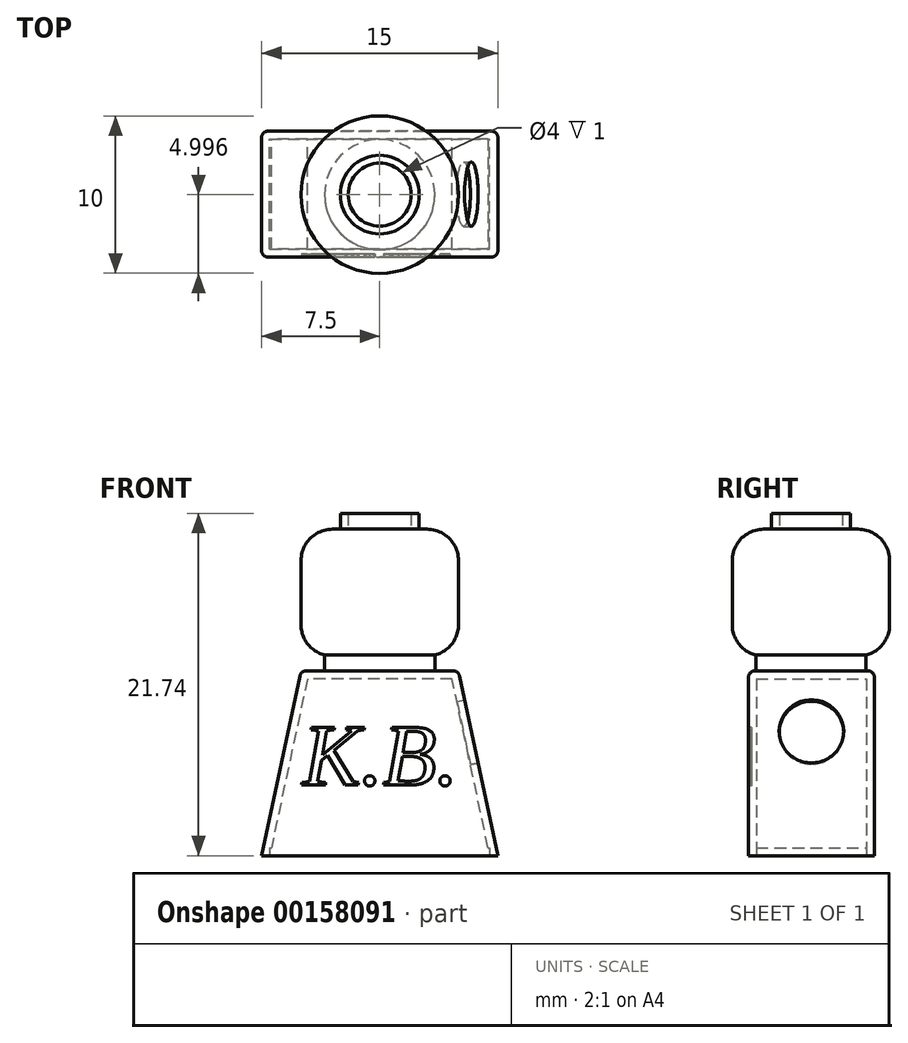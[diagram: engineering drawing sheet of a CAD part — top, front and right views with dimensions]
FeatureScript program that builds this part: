
annotation { "Feature Type Name" : "Feature", "Feature Type Description" : "" }
export const myFeature = defineFeature(function(context is Context, id is Id, definition is map)
    precondition{}
    {
        {
            var Q0;
            Q0=qCreatedBy(makeId("Front.planeOp"),FACE);
            var sketch = newSketch(context, id + "F0", { "sketchPlane" : qUnion([Q0])});
            skLineSegment(sketch, "E0", {"start": v(0, 11.74) * mm, "end": v(-5, 11.74) * mm});
            skLineSegment(sketch, "E1", {"start": v(-5, 11.74) * mm, "end": v(-7.5, 0) * mm});
            skLineSegment(sketch, "E2", {"start": v(-7.5, 0) * mm, "end": v(0, 0) * mm});
            skLineSegment(sketch, "E3", {"start": v(0, 0) * mm, "end": v(7.5, 0) * mm});
            skLineSegment(sketch, "E4", {"start": v(7.5, 0) * mm, "end": v(5, 11.74) * mm});
            skLineSegment(sketch, "E5", {"start": v(5, 11.74) * mm, "end": v(0, 11.74) * mm});
            skSolve(sketch);
        }
        {
            var Q0;
            Q0=makeQuery(id+"F0.imprint","IMPRINT",FACE,{"disambiguationData":[TD([[makeQuery(id+"F0.imprint","IMPRINT",EDGE,{"derivedFrom":sQuery(id+"F0.wireOp",EDGE,"E0")}),1.0]])]});
            extrude(context, id + "F1", {"entities" : qUnion([Q0]), "depth" : 8 * mm});
        }
        {
            var Q0;
            Q0=makeQuery(id+"F1.opExtrude","SWEPT_FACE",FACE,{"disambiguationData":[OSD([sQuery(id+"F0.wireOp",EDGE,"E2"),sQuery(id+"F0.wireOp",EDGE,"E3")])]});
            shell(context, id + "F2", {"entities" : qUnion([Q0]), "thickness" : 0.5 * mm});
        }
        {
            var Q0;
            Q0=makeQuery(id+"F1.opExtrude","SWEPT_FACE",FACE,{"disambiguationData":[OSD([sQuery(id+"F0.wireOp",EDGE,"E2"),sQuery(id+"F0.wireOp",EDGE,"E3")])]});
            var sketch = newSketch(context, id + "F3", { "sketchPlane" : qUnion([Q0])});
            skSolve(sketch);
        }
        {
            var Q0;
            {var subQ0=sQuery(id+"F0.wireOp",EDGE,"E2");Q0=makeQuery(id+"F3.imprint","IMPRINT",FACE,{"disambiguationData":[TD([[makeQuery(id+"F3.imprint","IMPRINT",EDGE,{"derivedFrom":makeQuery(id+"F2.opShell","OFFSET_EDGE",EDGE,{"disambiguationData":[OSD([sQuery(id+"F0.wireOp",EDGE,"E1"),subQ0])]})}),1.0]])]});}
            extrude(context, id + "F4", {"entities" : qUnion([Q0]), "operationType" : NewBodyOperationType.REMOVE, "oppositeDirection" : true, "depth" : 0.5 * mm});
        }
        {
            var Q0;
            Q0=makeQuery(id+"F1.opExtrude","CAP_EDGE",EDGE,{"disambiguationData":[OSD([sQuery(id+"F0.wireOp",EDGE,"E0"),sQuery(id+"F0.wireOp",EDGE,"E5")])],"isStart":true});
            var Q1;
            Q1=makeQuery(id+"F1.opExtrude","SWEPT_EDGE",EDGE,{"disambiguationData":[OSD([sQuery(id+"F0.wireOp",EDGE,"E0"),sQuery(id+"F0.wireOp",EDGE,"E1")])]});
            var Q2;
            Q2=makeQuery(id+"F1.opExtrude","CAP_EDGE",EDGE,{"disambiguationData":[OSD([sQuery(id+"F0.wireOp",EDGE,"E0"),sQuery(id+"F0.wireOp",EDGE,"E5")])],"isStart":false});
            var Q3;
            Q3=makeQuery(id+"F1.opExtrude","CAP_EDGE",EDGE,{"disambiguationData":[OSD([sQuery(id+"F0.wireOp",EDGE,"E4")])],"isStart":true});
            var Q4;
            Q4=makeQuery(id+"F1.opExtrude","SWEPT_EDGE",EDGE,{"disambiguationData":[OSD([sQuery(id+"F0.wireOp",EDGE,"E4"),sQuery(id+"F0.wireOp",EDGE,"E5")])]});
            var Q5;
            Q5=makeQuery(id+"F1.opExtrude","CAP_EDGE",EDGE,{"disambiguationData":[OSD([sQuery(id+"F0.wireOp",EDGE,"E4")])],"isStart":false});
            var Q6;
            Q6=makeQuery(id+"F1.opExtrude","CAP_EDGE",EDGE,{"disambiguationData":[OSD([sQuery(id+"F0.wireOp",EDGE,"E1")])],"isStart":true});
            var Q7;
            Q7=makeQuery(id+"F1.opExtrude","CAP_EDGE",EDGE,{"disambiguationData":[OSD([sQuery(id+"F0.wireOp",EDGE,"E1")])],"isStart":false});
            fillet(context, id + "F5", {"entities" : qUnion([Q0, Q1, Q2, Q3, Q4, Q5, Q6, Q7]), "radius" : 0.4 * mm, "tangentPropagation" : true, "allowEdgeOverflow" : false});
        }
        {
            var Q0;
            Q0=makeQuery(id+"F1.opExtrude","SWEPT_FACE",FACE,{"disambiguationData":[OSD([sQuery(id+"F0.wireOp",EDGE,"E4")])]});
            var sketch = newSketch(context, id + "F6", { "sketchPlane" : qUnion([Q0])});
            skCircle(sketch, "E6", {"center": v(-4, 6.51) * mm, "radius": 2.05 * mm});
            skSolve(sketch);
        }
        {
            var Q0;
            Q0=makeQuery(id+"F6.imprint","IMPRINT",FACE,{"disambiguationData":[TD([[makeQuery(id+"F6.imprint","IMPRINT",EDGE,{"derivedFrom":sQuery(id+"F6.wireOp",EDGE,"E6")}),1.0]])]});
            extrude(context, id + "F7", {"entities" : qUnion([Q0]), "operationType" : NewBodyOperationType.REMOVE, "oppositeDirection" : true, "depth" : 2 * mm});
        }
        {
            var Q0;
            Q0=makeQuery(id+"F1.opExtrude","SWEPT_FACE",FACE,{"disambiguationData":[OSD([sQuery(id+"F0.wireOp",EDGE,"E0"),sQuery(id+"F0.wireOp",EDGE,"E5")])]});
            var sketch = newSketch(context, id + "F8", { "sketchPlane" : qUnion([Q0])});
            skCircle(sketch, "E7", {"center": v(0, -4.03) * mm, "radius": 3.5 * mm});
            skSolve(sketch);
        }
        {
            var Q0;
            Q0=makeQuery(id+"F8.imprint","IMPRINT",FACE,{"disambiguationData":[TD([[makeQuery(id+"F8.imprint","IMPRINT",EDGE,{"derivedFrom":sQuery(id+"F8.wireOp",EDGE,"E7")}),1.0]])]});
            extrude(context, id + "F9", {"entities" : qUnion([Q0]), "depth" : 1 * mm});
        }
        {
            var Q0;
            Q0=makeQuery(id+"F9.opExtrude","CAP_FACE",FACE,{"disambiguationData":[OSD([sQuery(id+"F8.wireOp",EDGE,"E7")])],"isStart":false});
            var sketch = newSketch(context, id + "F10", { "sketchPlane" : qUnion([Q0])});
            skCircle(sketch, "E8", {"center": v(0, -4.03) * mm, "radius": 5 * mm});
            skSolve(sketch);
        }
        {
            var Q0;
            Q0=makeQuery(id+"F10.imprint","IMPRINT",FACE,{"disambiguationData":[TD([[makeQuery(id+"F10.imprint","IMPRINT",EDGE,{"derivedFrom":sQuery(id+"F10.wireOp",EDGE,"E8")}),1.0]])]});
            var Q1;
            Q1=makeQuery(id+"F10.imprint","IMPRINT",FACE,{"disambiguationData":[TD([[makeQuery(id+"F10.imprint","IMPRINT",EDGE,{"derivedFrom":makeQuery(id+"F9.opExtrude","CAP_EDGE",EDGE,{"disambiguationData":[OSD([sQuery(id+"F8.wireOp",EDGE,"E7")])],"isStart":false})}),1.0]])]});
            extrude(context, id + "F11", {"entities" : qUnion([Q0, Q1]), "operationType" : NewBodyOperationType.ADD, "depth" : 8 * mm});
        }
        {
            var Q0;
            Q0=makeQuery(id+"F11.opExtrude","CAP_FACE",FACE,{"disambiguationData":[OSD([sQuery(id+"F10.wireOp",EDGE,"E8")])],"isStart":false});
            var sketch = newSketch(context, id + "F12", { "sketchPlane" : qUnion([Q0])});
            skCircle(sketch, "E9", {"center": v(0, -4.03) * mm, "radius": 2 * mm});
            skCircle(sketch, "E10", {"center": v(0, -4.03) * mm, "radius": 2.5 * mm});
            skSolve(sketch);
        }
        {
            var Q0;
            Q0=makeQuery(id+"F12.imprint","IMPRINT",FACE,{"disambiguationData":[TD([[makeQuery(id+"F12.imprint","IMPRINT",EDGE,{"derivedFrom":sQuery(id+"F12.wireOp",EDGE,"E9")}),-1.0]])]});
            extrude(context, id + "F13", {"entities" : qUnion([Q0]), "depth" : 1 * mm});
        }
        {
            var Q0;
            Q0=makeQuery(id+"F11.opExtrude","CAP_EDGE",EDGE,{"disambiguationData":[OSD([sQuery(id+"F10.wireOp",EDGE,"E8")])],"isStart":false});
            var Q1;
            Q1=makeQuery(id+"F11.opExtrude","CAP_EDGE",EDGE,{"disambiguationData":[OSD([sQuery(id+"F10.wireOp",EDGE,"E8")])],"isStart":true});
            fillet(context, id + "F14", {"entities" : qUnion([Q0, Q1]), "radius" : 2 * mm, "tangentPropagation" : true, "allowEdgeOverflow" : false});
        }
        {
            var Q0;
            Q0=makeQuery(id+"F1.opExtrude","CAP_FACE",FACE,{"disambiguationData":[OSD([sQuery(id+"F0.wireOp",EDGE,"E0"),sQuery(id+"F0.wireOp",EDGE,"E1"),sQuery(id+"F0.wireOp",EDGE,"E2"),sQuery(id+"F0.wireOp",EDGE,"E3"),sQuery(id+"F0.wireOp",EDGE,"E4"),sQuery(id+"F0.wireOp",EDGE,"E5")])],"isStart":false});
            var sketch = newSketch(context, id + "F15", { "sketchPlane" : qUnion([Q0])});
            skText(sketch, "E11", { "text": "K.B.", "fontName": "Tinos-Italic.ttf"});
            const initialGuessF15  = {"E11": [-0.0049, 0.0045, 1, 0, 0.004]};
            skSetInitialGuess(sketch, initialGuessF15);
            skSolve(sketch);
        }
        {
            var Q0;
            Q0 = qSketchRegion(id + "F15", true);
            extrude(context, id + "F16", {"entities" : qUnion([Q0]), "operationType" : NewBodyOperationType.REMOVE, "oppositeDirection" : true, "depth" : 0.2 * mm});
        }
    });
